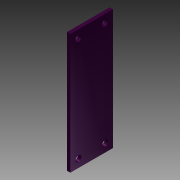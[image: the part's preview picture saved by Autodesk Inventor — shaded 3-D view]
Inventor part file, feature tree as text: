
AUTODESK INVENTOR PART (.ipt)
format: ipt  version: 2015 (Build 190159000, 159)  size: 102,912 bytes
history: native  units: in
note: dims shown in document units (in); Inventor stores cm internally (conversion verified against a paired STEP export)
features: extrude x1, sketch x1
ambient origin geometry x8: Origin, YZ Plane, XZ Plane, XY Plane, X Axis, Y Axis, Z Axis, Center Point
bodies: Solid1 (feature_tree)
feature tree (2):
  extrude  "Extrusion1"  Depth=0.8in
  sketch  "Sketch1"  dims[d0=2.25in d1=0.8in d2=0.8in d5=0.1102in d6=0.15in d7=0.15in d12=0.0646in d13=0.0in d14=0.1102in d15=0.5in d18=1.95in]
